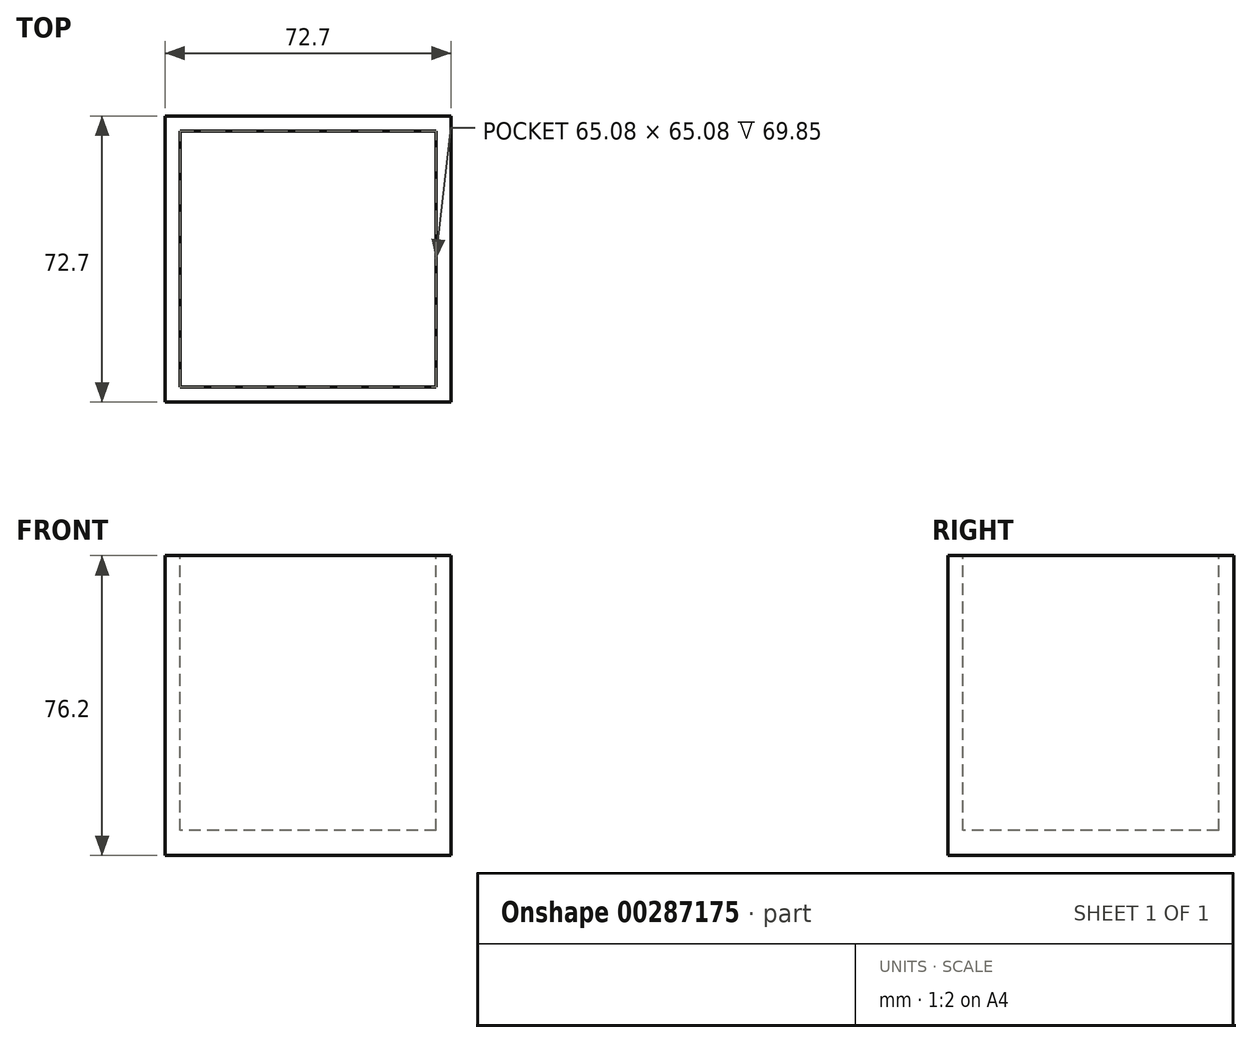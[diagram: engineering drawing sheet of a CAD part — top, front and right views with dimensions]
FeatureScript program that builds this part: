
annotation { "Feature Type Name" : "Feature", "Feature Type Description" : "" }
export const myFeature = defineFeature(function(context is Context, id is Id, definition is map)
    precondition{}
    {
        {
            var Q0;
            Q0=qCreatedBy(makeId("Top.planeOp"),FACE);
            var sketch = newSketch(context, id + "F0", { "sketchPlane" : qUnion([Q0])});
            skLineSegment(sketch, "E0.0", {"start": v(-31.78, 27.72) * mm, "end": v(-31.78, -44.98) * mm});
            skLineSegment(sketch, "E0.1", {"start": v(-31.78, 27.72) * mm, "end": v(40.92, 27.72) * mm});
            skLineSegment(sketch, "E0.2", {"start": v(40.92, 27.72) * mm, "end": v(40.92, -44.98) * mm});
            skLineSegment(sketch, "E0.3", {"start": v(-31.78, -44.98) * mm, "end": v(40.92, -44.98) * mm});
            skLineSegment(sketch, "E1", {"start": v(4.57, 27.72) * mm, "end": v(4.57, -44.98) * mm, "construction": true});
            skPoint(sketch, "E2", {"position": v(4.57, -8.63) * mm});
            skSolve(sketch);
        }
        {
            var Q0;
            Q0=makeQuery(id+"F0.imprint","IMPRINT",FACE,{"disambiguationData":[TD([[makeQuery(id+"F0.imprint","IMPRINT",EDGE,{"derivedFrom":sQuery(id+"F0.wireOp",EDGE,"E0.0")}),1.0]])]});
            extrude(context, id + "F1", {"entities" : qUnion([Q0]), "depth" : 76.2 * mm});
        }
        {
            var Q0;
            Q0=makeQuery(id+"F1.opExtrude","CAP_FACE",FACE,{"disambiguationData":[OSD([sQuery(id+"F0.wireOp",EDGE,"E0.0"),sQuery(id+"F0.wireOp",EDGE,"E0.1"),sQuery(id+"F0.wireOp",EDGE,"E0.2"),sQuery(id+"F0.wireOp",EDGE,"E0.3")])],"isStart":false});
            var sketch = newSketch(context, id + "F2", { "sketchPlane" : qUnion([Q0])});
            skLineSegment(sketch, "E3.0", {"start": v(-27.97, 23.91) * mm, "end": v(-27.97, -41.17) * mm});
            skLineSegment(sketch, "E3.1", {"start": v(37.11, 23.91) * mm, "end": v(-27.97, 23.91) * mm});
            skLineSegment(sketch, "E3.2", {"start": v(37.11, -41.17) * mm, "end": v(37.11, 23.91) * mm});
            skLineSegment(sketch, "E3.3", {"start": v(-27.97, -41.17) * mm, "end": v(37.11, -41.17) * mm});
            skSolve(sketch);
        }
        {
            var Q0;
            Q0 = qSketchRegion(id + "F2", true);
            extrude(context, id + "F3", {"entities" : qUnion([Q0]), "operationType" : NewBodyOperationType.REMOVE, "oppositeDirection" : true, "depth" : 69.85 * mm});
        }
    });
